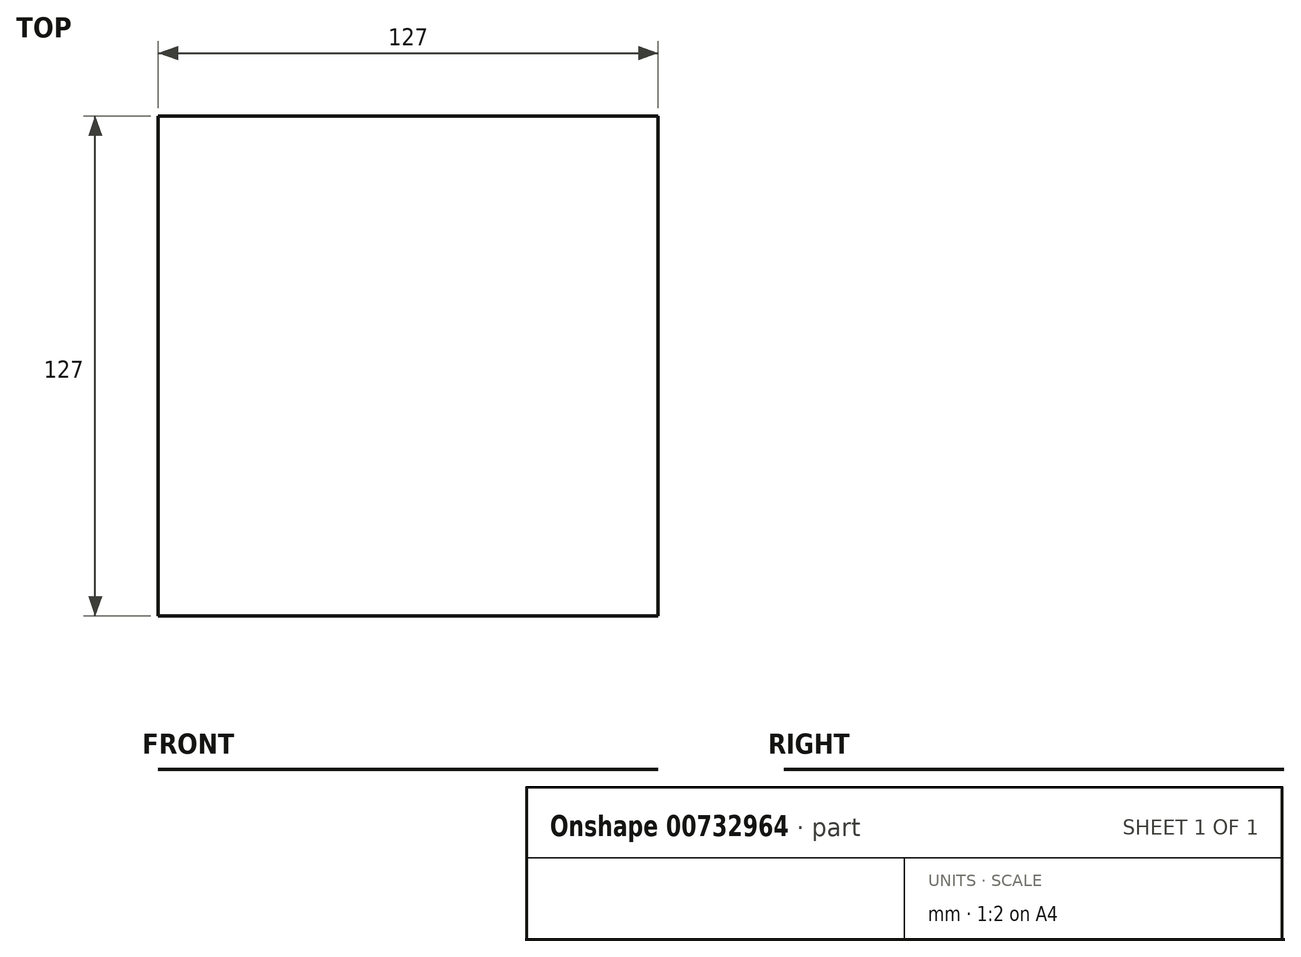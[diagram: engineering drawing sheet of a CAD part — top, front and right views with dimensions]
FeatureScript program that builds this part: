
annotation { "Feature Type Name" : "Feature", "Feature Type Description" : "" }
export const myFeature = defineFeature(function(context is Context, id is Id, definition is map)
    precondition{}
    {
        {
            var Q0;
            Q0=qCreatedBy(makeId("Top.planeOp"),FACE);
            var sketch = newSketch(context, id + "F0", { "sketchPlane" : qUnion([Q0])});
            skLineSegment(sketch, "E0.bottom", {"start": v(0, 0) * mm, "end": v(-127, 0) * mm});
            skLineSegment(sketch, "E0.top", {"start": v(0, -127) * mm, "end": v(-127, -127) * mm});
            skLineSegment(sketch, "E0.left", {"start": v(0, 0) * mm, "end": v(0, -127) * mm});
            skLineSegment(sketch, "E0.right", {"start": v(-127, 0) * mm, "end": v(-127, -127) * mm});
            skSolve(sketch);
        }
        {
            var Q0;
            Q0=makeQuery(id+"F0.imprint","IMPRINT",FACE,{"disambiguationData":[TD([[makeQuery(id+"F0.imprint","IMPRINT",EDGE,{"derivedFrom":sQuery(id+"F0.wireOp",EDGE,"E0.bottom")}),1.0]])]});
            extrude(context, id + "F1", {"entities" : qUnion([Q0]), "depth" : 1 / 203.2 * mm, "offsetDistance" : 25.4 * mm});
        }
    });
